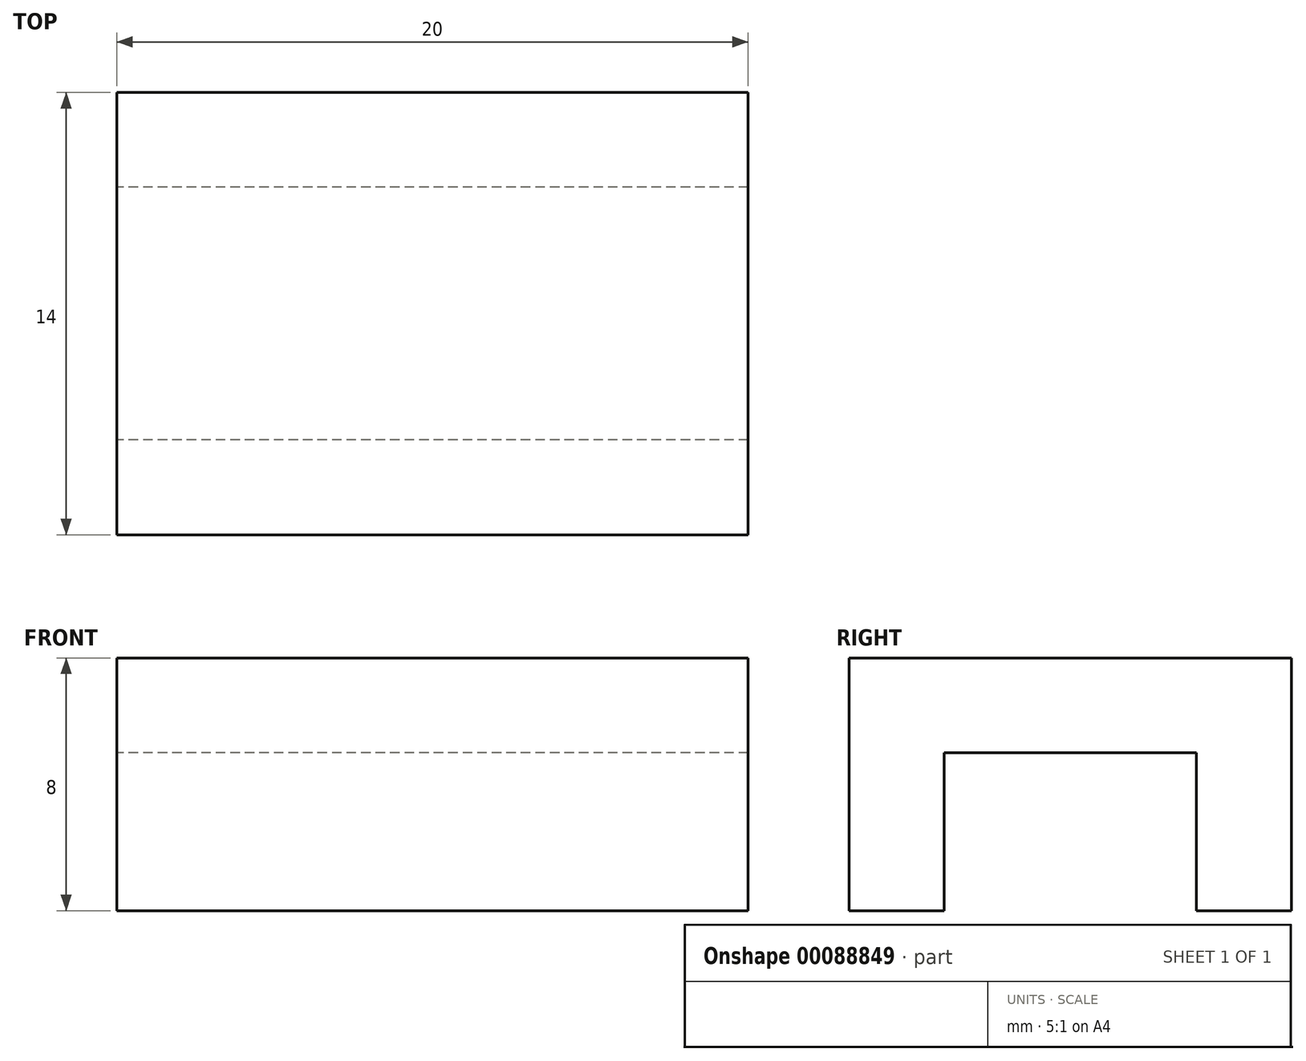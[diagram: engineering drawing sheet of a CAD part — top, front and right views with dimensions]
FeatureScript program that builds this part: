
annotation { "Feature Type Name" : "Feature", "Feature Type Description" : "" }
export const myFeature = defineFeature(function(context is Context, id is Id, definition is map)
    precondition{}
    {
        {
            var Q0;
            Q0=qCreatedBy(makeId("Front.planeOp"),FACE);
            var sketch = newSketch(context, id + "F0", { "sketchPlane" : qUnion([Q0])});
            skLineSegment(sketch, "E0.bottom", {"start": v(-16, 8) * mm, "end": v(16, 8) * mm});
            skLineSegment(sketch, "E0.top", {"start": v(-16, -8) * mm, "end": v(16, -8) * mm});
            skArc(sketch, "E1", {"start": v(-16, 8) * mm, "mid": v(-24, 0) * mm, "end": v(-16, -8) * mm});
            skArc(sketch, "E2", {"start": v(16, -8) * mm, "mid": v(24, 0) * mm, "end": v(16, 8) * mm});
            skLineSegment(sketch, "E3", {"start": v(-16, 0) * mm, "end": v(16, 0) * mm, "construction": true});
            skCircle(sketch, "E4", {"center": v(-16, 0) * mm, "radius": 3 * mm});
            skCircle(sketch, "E5.MirrorC", {"center": v(16, 0) * mm, "radius": 3 * mm});
            skLineSegment(sketch, "E6.bottom", {"start": v(16, 8) * mm, "end": v(-4, 8) * mm});
            skLineSegment(sketch, "E6.top", {"start": v(16, 16) * mm, "end": v(-4, 16) * mm});
            skLineSegment(sketch, "E6.left", {"start": v(16, 8) * mm, "end": v(16, 16) * mm});
            skLineSegment(sketch, "E6.right", {"start": v(-4, 8) * mm, "end": v(-4, 16) * mm});
            skSolve(sketch);
        }
        {
            var Q0;
            Q0 = qSketchRegion(id + "F0", true);
            var Q1;
            Q1=makeQuery(id+"F0.imprint","IMPRINT",FACE,{"disambiguationData":[TD([[makeQuery(id+"F0.imprint","IMPRINT",EDGE,{"derivedFrom":sQuery(id+"F0.wireOp",EDGE,"E4")}),1.0]])]});
            var Q2;
            Q2=makeQuery(id+"F0.imprint","IMPRINT",FACE,{"disambiguationData":[TD([[makeQuery(id+"F0.imprint","IMPRINT",EDGE,{"derivedFrom":sQuery(id+"F0.wireOp",EDGE,"E5.MirrorC")}),-1.0]])]});
            extrude(context, id + "F1", {"entities" : qUnion([Q0, Q1, Q2]), "depth" : 14 * mm});
        }
        {
            var Q0;
            Q0=makeQuery(id+"F1.opExtrude","SWEPT_FACE",FACE,{"disambiguationData":[OSD([sQuery(id+"F0.wireOp",EDGE,"E6.right")])]});
            var Q1;
            Q1=makeQuery(id+"F1.opExtrude","SWEPT_FACE",FACE,{"disambiguationData":[OSD([sQuery(id+"F0.wireOp",EDGE,"E0.bottom")])]});
            var Q2;
            Q2=makeQuery(id+"F1.opExtrude","SWEPT_FACE",FACE,{"disambiguationData":[OSD([sQuery(id+"F0.wireOp",EDGE,"E1")])]});
            var Q3;
            Q3=makeQuery(id+"F1.opExtrude","SWEPT_FACE",FACE,{"disambiguationData":[OSD([sQuery(id+"F0.wireOp",EDGE,"E0.top")])]});
            var Q4;
            Q4=makeQuery(id+"F1.opExtrude","SWEPT_FACE",FACE,{"disambiguationData":[OSD([sQuery(id+"F0.wireOp",EDGE,"E2")])]});
            var Q5;
            Q5=makeQuery(id+"F1.opExtrude","SWEPT_FACE",FACE,{"disambiguationData":[OSD([sQuery(id+"F0.wireOp",EDGE,"E6.left")])]});
            shell(context, id + "F2", {"entities" : qUnion([Q0, Q1, Q2, Q3, Q4, Q5]), "thickness" : 3 * mm});
        }
        {
            var Q0;
            Q0=makeQuery(id+"F0.imprint","IMPRINT",FACE,{"disambiguationData":[TD([[makeQuery(id+"F0.imprint","IMPRINT",EDGE,{"derivedFrom":sQuery(id+"F0.wireOp",EDGE,"E5.MirrorC")}),-1.0]])]});
            var Q1;
            Q1=makeQuery(id+"F0.imprint","IMPRINT",FACE,{"disambiguationData":[TD([[makeQuery(id+"F0.imprint","IMPRINT",EDGE,{"derivedFrom":sQuery(id+"F0.wireOp",EDGE,"E4")}),1.0]])]});
            extrude(context, id + "F3", {"entities" : qUnion([Q0, Q1]), "operationType" : NewBodyOperationType.REMOVE, "depth" : 14 * mm});
        }
    });
